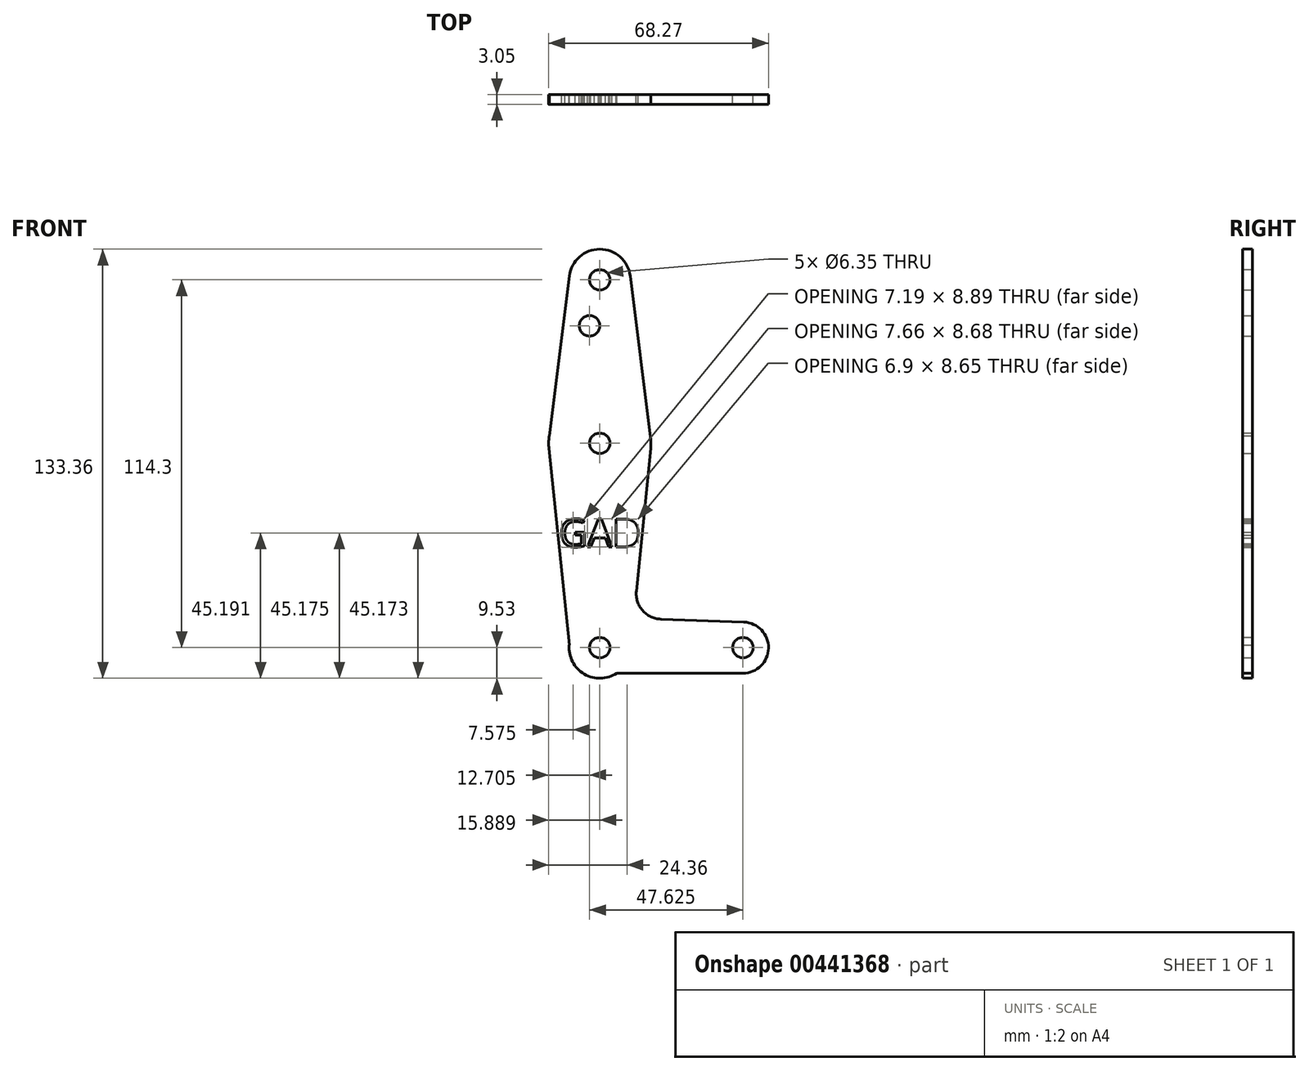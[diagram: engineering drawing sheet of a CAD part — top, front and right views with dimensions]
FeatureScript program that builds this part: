
annotation { "Feature Type Name" : "Feature", "Feature Type Description" : "" }
export const myFeature = defineFeature(function(context is Context, id is Id, definition is map)
    precondition{}
    {
        {
            var Q0;
            Q0=qCreatedBy(makeId("Front.planeOp"),FACE);
            var sketch = newSketch(context, id + "F0", { "sketchPlane" : qUnion([Q0])});
            skLineSegment(sketch, "E0", {"start": v(0, 0) * mm, "end": v(0, 114.3) * mm, "construction": true});
            skCircle(sketch, "E1", {"center": v(0, 0) * mm, "radius": 9.53 * mm});
            skCircle(sketch, "E2", {"center": v(0, 63.5) * mm, "radius": 15.88 * mm});
            skCircle(sketch, "E3", {"center": v(0, 114.3) * mm, "radius": 9.53 * mm});
            skLineSegment(sketch, "E4", {"start": v(0, 0) * mm, "end": v(44.45, 0) * mm, "construction": true});
            skCircle(sketch, "E5", {"center": v(44.45, 0) * mm, "radius": 7.94 * mm});
            skLineSegment(sketch, "E6", {"start": v(-9.45, 115.49) * mm, "end": v(-15.8, 65.13) * mm});
            skLineSegment(sketch, "E7", {"start": v(9.45, 115.5) * mm, "end": v(15.8, 65.13) * mm});
            skLineSegment(sketch, "E8", {"start": v(-15.8, 61.87) * mm, "end": v(-9.5, 0.77) * mm});
            skLineSegment(sketch, "E9", {"start": v(15.8, 61.91) * mm, "end": v(11.34, 17.6) * mm});
            skLineSegment(sketch, "E10", {"start": v(5.27, -7.94) * mm, "end": v(44.45, -7.94) * mm});
            skLineSegment(sketch, "E11", {"start": v(18.97, 8.85) * mm, "end": v(44.73, 7.93) * mm});
            skCircle(sketch, "E12", {"center": v(0, 114.3) * mm, "radius": 3.18 * mm});
            skCircle(sketch, "E13", {"center": v(0, 63.5) * mm, "radius": 3.18 * mm});
            skCircle(sketch, "E14", {"center": v(0, 0) * mm, "radius": 3.18 * mm});
            skCircle(sketch, "E15", {"center": v(44.45, 0) * mm, "radius": 3.18 * mm});
            skCircle(sketch, "E16", {"center": v(-3.18, 100.03) * mm, "radius": 3.18 * mm});
            skArc(sketch, "E17.filletArc", {"start": v(11.34, 17.6) * mm, "mid": v(13.26, 11.57) * mm, "end": v(18.97, 8.85) * mm});
            skText(sketch, "E18", { "text": "GAD\n", "fontName": "OpenSans-Regular.ttf"});
            skPoint(sketch, "E18.firstSnap0", {"position": v(-12.64, 31.32) * mm});
            skPoint(sketch, "E18.secondSnap0", {"position": v(-12.64, 31.32) * mm});
            const initialGuessF0  = {"E18": [-0.01264, 0.03132, 1, 0, 0.00872]};
            skSetInitialGuess(sketch, initialGuessF0);
            skSolve(sketch);
        }
        {
            var Q0;
            Q0 = qSketchRegion(id + "F0", true);
            extrude(context, id + "F1", {"entities" : qUnion([Q0]), "depth" : 3.05 * mm});
        }
    });
